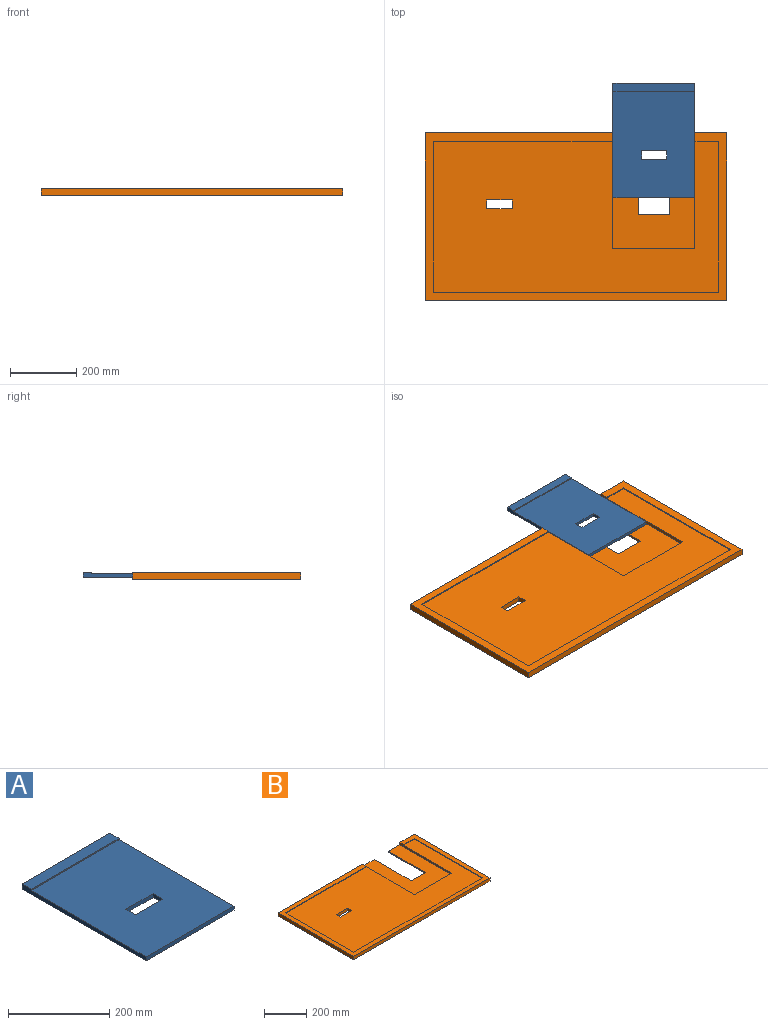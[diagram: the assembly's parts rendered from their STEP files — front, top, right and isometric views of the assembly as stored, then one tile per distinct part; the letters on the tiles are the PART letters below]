
ASSEMBLY  parts=2 mates=1
PART A: 12 faces, bbox 245.7x346.7x12.7 mm
  f0: plane 76.2x9.53mm, normal (0,-1,0), area 725.8mm2, adj f1,f3,f4,f11
  f1: plane 26.99x9.53mm, normal (1,0,0), area 257.1mm2, adj f0,f2,f4,f11
  f2: plane 76.2x9.53mm, normal (0,1,0), area 725.8mm2, adj f1,f3,f4,f11
  f3: plane 26.99x9.53mm, normal (-1,0,0), area 257.1mm2, adj f0,f2,f4,f11
  f4: plane 321.31x245.75mm, normal (0,0,1), area 76903.9mm2, adj f0,f1,f2,f3,f5,f6,f9,f10
  f5: plane 245.75x9.53mm, normal (0,-1,0), area 2340.7mm2, adj f4,f6,f9,f11
  f6: plane 346.71x12.7mm, normal (1,0,0), area 3383.1mm2, adj f4,f5,f7,f8,f10,f11
  f7: plane 245.75x25.4mm, normal (0,0,1), area 6241.9mm2, adj f6,f8,f9,f10
  f8: plane 245.75x12.7mm, normal (0,1,0), area 3121mm2, adj f6,f7,f9,f11
  f9: plane 346.71x12.7mm, normal (-1,0,0), area 3383.1mm2, adj f4,f5,f7,f8,f10,f11
  f10: plane 245.75x3.18mm, normal (0,-1,0), area 780.2mm2, adj f4,f6,f7,f9
  f11: plane 346.71x245.75mm, normal (0,0,-1), area 83145.8mm2, adj f0,f1,f2,f3,f5,f6,f8,f9
PART B: 24 faces, bbox 914.4x508x19.1 mm
  f0: plane 914.4x508mm, normal (0,0,-1), area 438870.1mm2, adj f5,f6,f7,f8,f9,f16,f17,f18
  f1: plane 863.6x457.2mm, normal (0,0,1), area 311551.8mm2, adj f2,f3,f10,f11,f12,f13,f14,f15
  f2: plane 349.25x12.7mm, normal (-1,0,0), area 3407.3mm2, adj f1,f3,f4,f9,f15,f23
  f3: plane 250.83x9.53mm, normal (0,1,0), area 2389.1mm2, adj f1,f2,f10,f23
  f4: plane 914.4x508mm, normal (0,0,1), area 63306.3mm2, adj f2,f5,f6,f7,f8,f9,f10,f11
  f5: plane 646.11x19.05mm, normal (0,1,0), area 11300.4mm2, adj f0,f4,f6,f10,f20,f23
  f6: plane 508x19.05mm, normal (-1,0,0), area 9677.4mm2, adj f0,f4,f5,f7
  f7: plane 914.4x19.05mm, normal (0,-1,0), area 17419.3mm2, adj f0,f4,f6,f8
  f8: plane 508x19.05mm, normal (1,0,0), area 9677.4mm2, adj f0,f4,f7,f9
  f9: plane 173.04x19.05mm, normal (0,1,0), area 2328.6mm2, adj f0,f2,f4,f8,f22,f23
  f10: plane 349.25x12.7mm, normal (1,0,0), area 3407.3mm2, adj f1,f3,f4,f5,f11,f23
  f11: plane 541.34x3.18mm, normal (0,-1,0), area 1718.7mm2, adj f1,f4,f10,f12
  f12: plane 457.2x3.18mm, normal (1,0,0), area 1451.6mm2, adj f1,f4,f11,f13
  f13: plane 863.6x3.18mm, normal (0,1,0), area 2741.9mm2, adj f1,f4,f12,f14
  f14: plane 457.2x3.18mm, normal (-1,0,0), area 1451.6mm2, adj f1,f4,f13,f15
  f15: plane 71.44x3.18mm, normal (0,-1,0), area 226.8mm2, adj f1,f2,f4,f14
  f16: plane 76.2x15.88mm, normal (0,-1,0), area 1209.7mm2, adj f0,f1,f17,f19
  f17: plane 26.99x15.88mm, normal (1,0,0), area 428.4mm2, adj f0,f1,f16,f18
  f18: plane 76.2x15.88mm, normal (0,1,0), area 1209.7mm2, adj f0,f1,f17,f19
  f19: plane 26.99x15.88mm, normal (-1,0,0), area 428.4mm2, adj f0,f1,f16,f18
  f20: plane 247.65x6.35mm, normal (1,0,0), area 1572.6mm2, adj f0,f5,f21,f23
  f21: plane 95.25x6.35mm, normal (0,1,0), area 604.8mm2, adj f0,f20,f22,f23
  f22: plane 247.65x6.35mm, normal (-1,0,0), area 1572.6mm2, adj f0,f9,f21,f23
  f23: plane 349.25x250.83mm, normal (0,0,1), area 64012mm2, adj f2,f3,f5,f9,f10,f20,f21,f22
PLACE A t=(229.3,239.84,-9.41)mm
PLACE B t=(14.79,-10.15,-9.41)mm fixed
MATE slider B.f3 <-> A.f5  axis (0,-1,0) through (234.92,-95.19,1.7)mm
